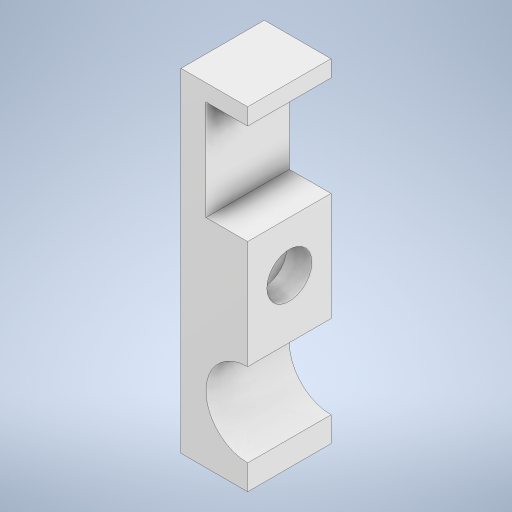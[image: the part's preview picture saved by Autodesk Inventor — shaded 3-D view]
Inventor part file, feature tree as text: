
AUTODESK INVENTOR PART (.ipt)
format: ipt  version: 2023 (Build 270158000, 158)  size: 280,064 bytes
history: native  units: mm
features: extrude x3, sketch x3
ambient origin geometry x8: Origin, YZ Plane, XZ Plane, XY Plane, X Axis, Y Axis, Z Axis, Center Point
bodies: Solid1 (feature_tree)
feature tree (6):
  extrude  "Extrusion1"  Depth=4.0mm
  extrude  "Extrusion2"  Depth=5.0mm
  extrude  "Extrusion3"  Depth=4.0mm
  sketch  "Sketch1"  dims[d0=20.0mm d1=4.0mm]
  sketch  "Sketch3"  dims[d2=5.0mm d3=5.0mm]
  sketch  "Sketch4"  dims[d4=4.0mm d5=4.0mm d6=3.0mm d7=3.0mm d8=5.0mm d9=0.0mm d10=10.0mm d11=2.5mm d12=20.0mm d13=2.7mm d14=20.0mm d15=0.0mm d16=4.9mm d17=2.5mm d18=0.0mm]
